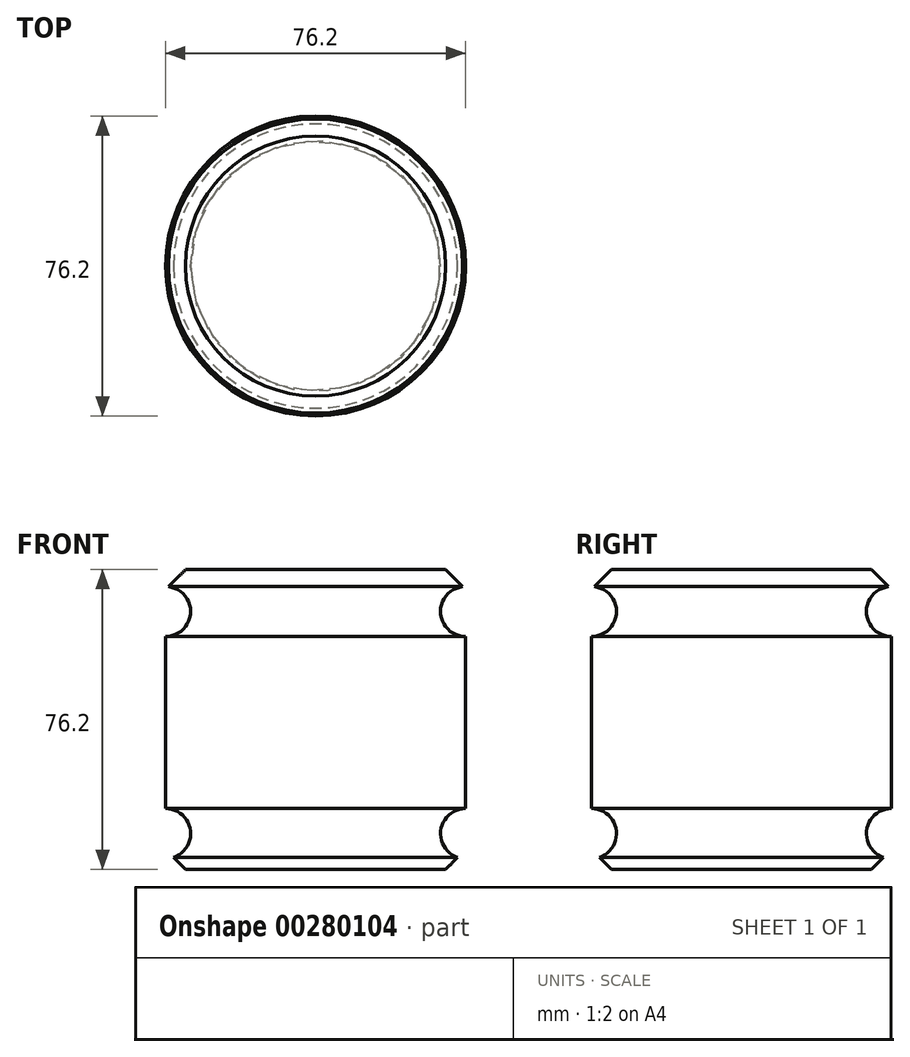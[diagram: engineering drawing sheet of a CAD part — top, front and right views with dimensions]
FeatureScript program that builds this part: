
annotation { "Feature Type Name" : "Feature", "Feature Type Description" : "" }
export const myFeature = defineFeature(function(context is Context, id is Id, definition is map)
    precondition{}
    {
        {
            var Q0;
            Q0=qCreatedBy(makeId("Front.planeOp"),FACE);
            var sketch = newSketch(context, id + "F0", { "sketchPlane" : qUnion([Q0])});
            skLineSegment(sketch, "E0", {"start": v(8, 0) * mm, "end": v(8, 76.2) * mm});
            skLineSegment(sketch, "E1", {"start": v(8, 76.2) * mm, "end": v(-30.1, 76.2) * mm});
            skLineSegment(sketch, "E2", {"start": v(-30.1, 76.2) * mm, "end": v(-30.1, 71.89) * mm});
            skLineSegment(sketch, "E3", {"start": v(-30.1, 0) * mm, "end": v(8, 0) * mm});
            skArc(sketch, "E4", {"start": v(-30.1, 59.19) * mm, "mid": v(-23.75, 65.54) * mm, "end": v(-30.1, 71.89) * mm});
            skArc(sketch, "E5", {"start": v(-30.1, 2.74) * mm, "mid": v(-23.75, 9.1) * mm, "end": v(-30.1, 15.44) * mm});
            skLineSegment(sketch, "E6.trimOffspring", {"start": v(-30.1, 59.19) * mm, "end": v(-30.1, 15.44) * mm});
            skLineSegment(sketch, "E7.trimOffspring", {"start": v(-30.1, 2.74) * mm, "end": v(-30.1, 0) * mm});
            skSolve(sketch);
        }
        {
            var Q0;
            Q0=makeQuery(id+"F0.imprint","IMPRINT",FACE,{"disambiguationData":[TD([[makeQuery(id+"F0.imprint","IMPRINT",EDGE,{"derivedFrom":sQuery(id+"F0.wireOp",EDGE,"E0")}),1.0]])]});
            var sketch = newSketch(context, id + "F1", { "sketchPlane" : qUnion([Q0])});
            skSolve(sketch);
        }
        {
            var Q0;
            Q0 = qSketchRegion(id + "F1", true);
            var Q1;
            Q1=makeQuery(id+"F0.imprint","IMPRINT",FACE,{"disambiguationData":[TD([[makeQuery(id+"F0.imprint","IMPRINT",EDGE,{"derivedFrom":sQuery(id+"F0.wireOp",EDGE,"E0")}),1.0]])]});
            var Q2;
            Q2=sQuery(id+"F0.wireOp",EDGE,"E0");
            revolve(context, id + "F2", {"entities" : qUnion([Q0, Q1]), "axis" : qUnion([Q2]), "revolveType" : RevolveType.FULL});
        }
        {
            var Q0;
            Q0=makeQuery(id+"F2.opRevolve","SWEPT_FACE",FACE,{"disambiguationData":[OSD([sQuery(id+"F0.wireOp",EDGE,"E1")])]});
            var Q1;
            Q1=makeQuery(id+"F2.opRevolve","SWEPT_FACE",FACE,{"disambiguationData":[OSD([sQuery(id+"F0.wireOp",EDGE,"E3")])]});
            chamfer(context, id + "F3", {"entities" : qUnion([Q0, Q1]), "width" : 5.08 * mm, "tangentPropagation" : true});
        }
    });
